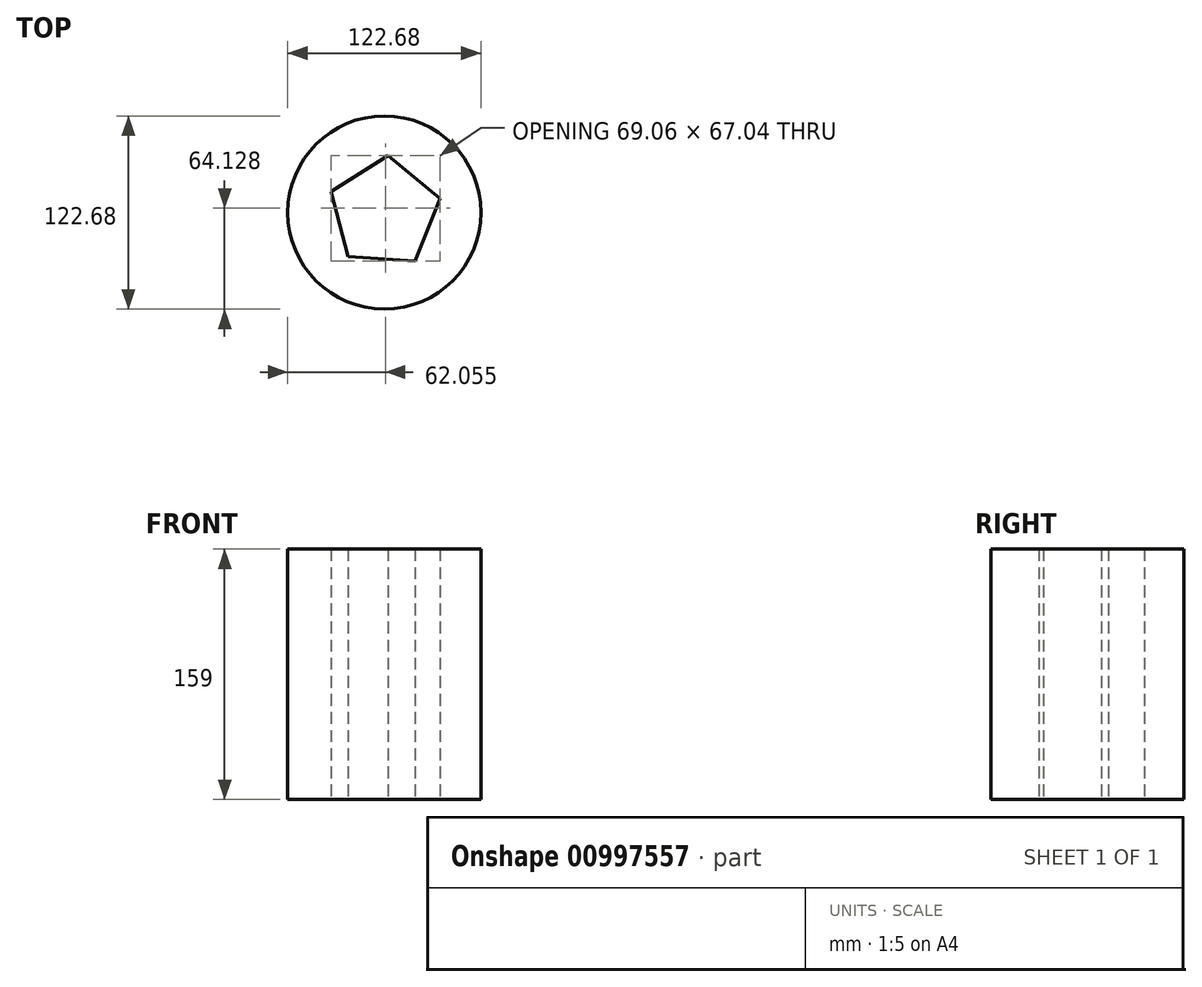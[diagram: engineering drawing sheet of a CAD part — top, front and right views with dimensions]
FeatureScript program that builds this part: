
annotation { "Feature Type Name" : "Feature", "Feature Type Description" : "" }
export const myFeature = defineFeature(function(context is Context, id is Id, definition is map)
    precondition{}
    {
        {
            var Q0;
            Q0=qCreatedBy(makeId("Top.planeOp"),FACE);
            var sketch = newSketch(context, id + "F0", { "sketchPlane" : qUnion([Q0])});
            skCircle(sketch, "E0", {"center": v(0, 0) * mm, "radius": 61.34 * mm});
            skSolve(sketch);
        }
        {
            var Q0;
            Q0=makeQuery(id+"F0.imprint","IMPRINT",FACE,{"disambiguationData":[TD([[makeQuery(id+"F0.imprint","IMPRINT",EDGE,{"derivedFrom":sQuery(id+"F0.wireOp",EDGE,"E0")}),1.0]])]});
            extrude(context, id + "F1", {"entities" : qUnion([Q0]), "depth" : 159 * mm, "offsetDistance" : 25.4 * mm});
        }
        {
            var Q0;
            Q0=qCreatedBy(makeId("Top.planeOp"),FACE);
            var sketch = newSketch(context, id + "F2", { "sketchPlane" : qUnion([Q0])});
            skCircle(sketch, "E1.cCircle", {"center": v(0, 0) * mm, "radius": 29.43 * mm, "construction": true});
            skLineSegment(sketch, "E1.0", {"start": v(2.31, 36.3) * mm, "end": v(35.25, 9.02) * mm});
            skLineSegment(sketch, "E1.1", {"start": v(35.25, 9.02) * mm, "end": v(19.47, -30.73) * mm});
            skLineSegment(sketch, "E1.2", {"start": v(19.47, -30.73) * mm, "end": v(-23.21, -28.02) * mm});
            skLineSegment(sketch, "E1.3", {"start": v(-23.21, -28.02) * mm, "end": v(-33.82, 13.42) * mm});
            skLineSegment(sketch, "E1.4", {"start": v(-33.82, 13.42) * mm, "end": v(2.31, 36.3) * mm});
            skPoint(sketch, "E1.0.midPoint", {"position": v(18.78, 22.66) * mm});
            skSolve(sketch);
        }
        {
            var Q0;
            Q0 = qSketchRegion(id + "F2", true);
            extrude(context, id + "F3", {"entities" : qUnion([Q0]), "operationType" : NewBodyOperationType.REMOVE, "endBound" : BoundingType.THROUGH_ALL, "depth" : 25.4 * mm, "offsetDistance" : 25.4 * mm});
        }
    });
